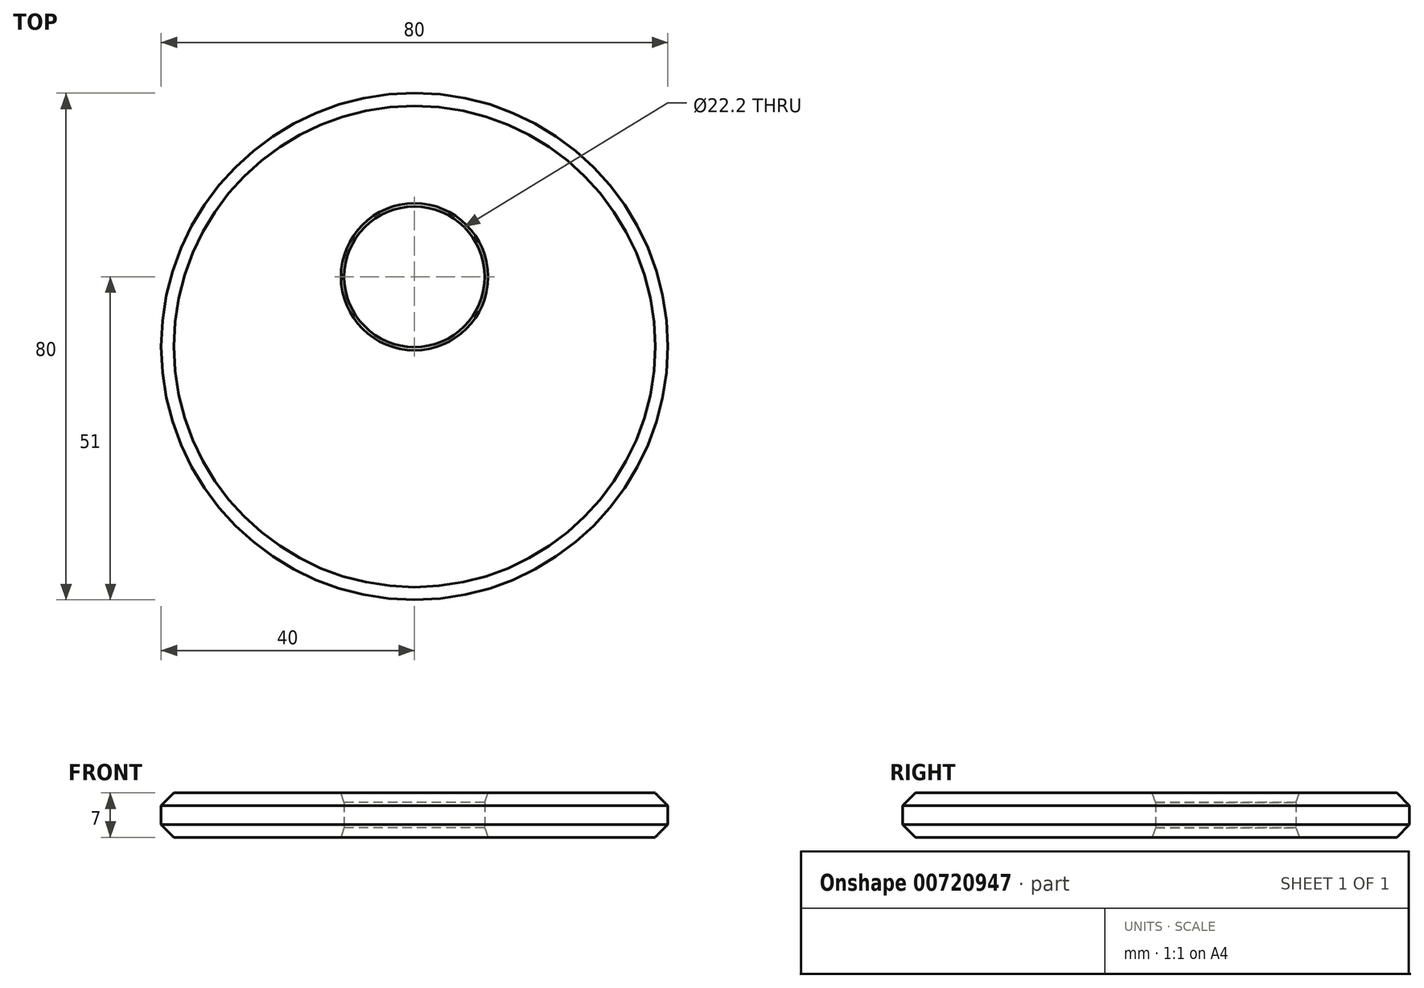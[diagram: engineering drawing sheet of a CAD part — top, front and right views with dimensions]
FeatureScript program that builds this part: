
annotation { "Feature Type Name" : "Feature", "Feature Type Description" : "" }
export const myFeature = defineFeature(function(context is Context, id is Id, definition is map)
    precondition{}
    {
        {
            var Q0;
            Q0=qCreatedBy(makeId("Top.planeOp"),FACE);
            var sketch = newSketch(context, id + "F0", { "sketchPlane" : qUnion([Q0])});
            skCircle(sketch, "E0", {"center": v(0, 0) * mm, "radius": 40 * mm});
            skLineSegment(sketch, "E1", {"start": v(0, 0) * mm, "end": v(0, 11) * mm, "construction": true});
            skCircle(sketch, "E2", {"center": v(0, 11) * mm, "radius": 11.1 * mm});
            skSolve(sketch);
        }
        {
            var Q0;
            Q0=makeQuery(id+"F0.imprint","IMPRINT",FACE,{"disambiguationData":[TD([[makeQuery(id+"F0.imprint","IMPRINT",EDGE,{"derivedFrom":sQuery(id+"F0.wireOp",EDGE,"E0")}),1.0]])]});
            extrude(context, id + "F1", {"entities" : qUnion([Q0]), "depth" : 7 * mm});
        }
        {
            var Q0;
            Q0=makeQuery(id+"F1.opExtrude","CAP_EDGE",EDGE,{"disambiguationData":[OSD([sQuery(id+"F0.wireOp",EDGE,"E0")])],"isStart":false});
            var Q1;
            Q1=makeQuery(id+"F1.opExtrude","CAP_EDGE",EDGE,{"disambiguationData":[OSD([sQuery(id+"F0.wireOp",EDGE,"E0")])],"isStart":true});
            chamfer(context, id + "F2", {"entities" : qUnion([Q0, Q1]), "width" : 2 * mm, "tangentPropagation" : true});
        }
        {
            var Q0;
            Q0=makeQuery(id+"F1.opExtrude","CAP_EDGE",EDGE,{"disambiguationData":[OSD([sQuery(id+"F0.wireOp",EDGE,"E2")])],"isStart":true});
            var Q1;
            Q1=makeQuery(id+"F1.opExtrude","CAP_EDGE",EDGE,{"disambiguationData":[OSD([sQuery(id+"F0.wireOp",EDGE,"E2")])],"isStart":false});
            chamfer(context, id + "F3", {"entities" : qUnion([Q0, Q1]), "chamferType" : ChamferType.TWO_OFFSETS, "width1" : .5 * mm, "oppositeDirection" : false, "width2" : 1.5 * mm, "tangentPropagation" : true});
        }
    });
